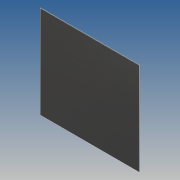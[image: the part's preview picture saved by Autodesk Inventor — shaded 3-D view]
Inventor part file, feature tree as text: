
AUTODESK INVENTOR PART (.ipt)
format: ipt  version: 2019 (Build 230136000, 136)  size: 79,872 bytes
history: native  units: mm
features: extrude x1, sketch x1
ambient origin geometry x8: Origin, YZ Plane, XZ Plane, XY Plane, X Axis, Y Axis, Z Axis, Center Point
bodies: Solid1 (feature_tree)
feature tree (2):
  extrude  "Extrusion1"  Depth=387.0mm
  sketch  "Sketch1"  dims[d0=362.0mm d1=387.0mm d2=2.0mm d3=0.0mm]
